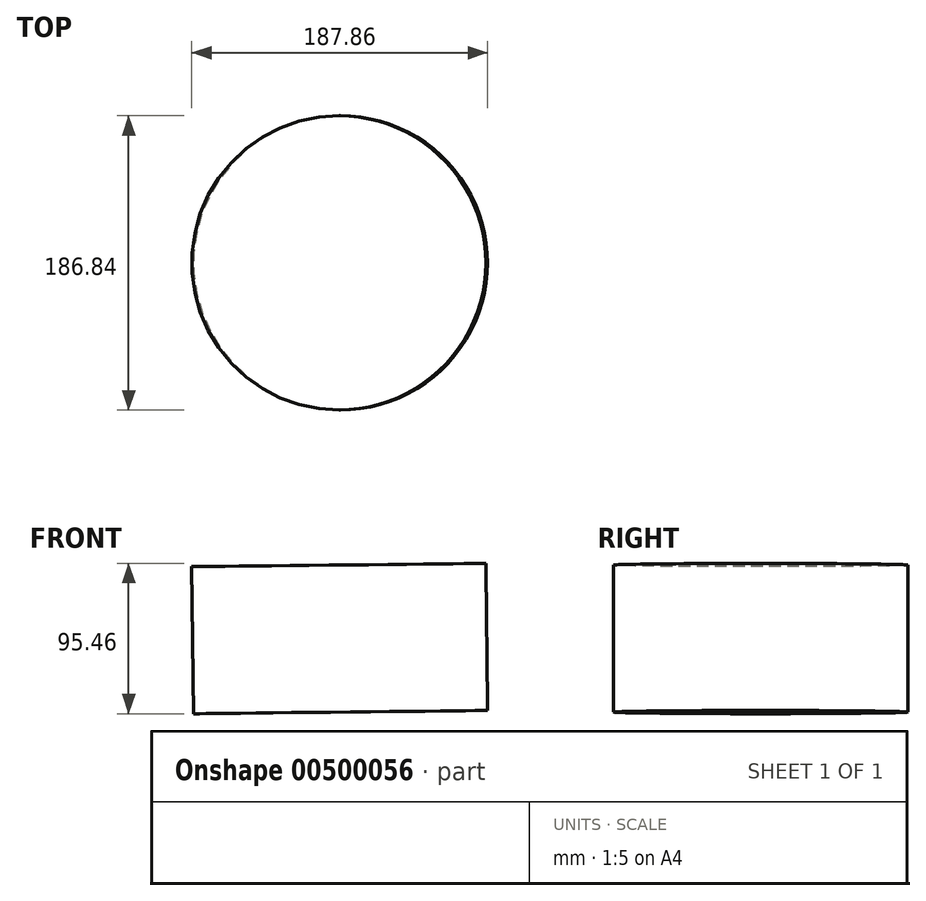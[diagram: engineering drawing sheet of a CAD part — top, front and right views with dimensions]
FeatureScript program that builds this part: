
annotation { "Feature Type Name" : "Feature", "Feature Type Description" : "" }
export const myFeature = defineFeature(function(context is Context, id is Id, definition is map)
    precondition{}
    {
        {
            var Q0;
            Q0=qCreatedBy(makeId("Front.planeOp"),FACE);
            var sketch = newSketch(context, id + "F0", { "sketchPlane" : qUnion([Q0])});
            skCircle(sketch, "E0.cCircle", {"center": v(0, 0) * mm, "radius": 66.06 * mm, "construction": true});
            skLineSegment(sketch, "E0.0", {"start": v(46.2, 47.22) * mm, "end": v(47.22, -46.2) * mm});
            skLineSegment(sketch, "E0.1", {"start": v(47.22, -46.2) * mm, "end": v(-46.2, -47.22) * mm});
            skLineSegment(sketch, "E0.2", {"start": v(-46.2, -47.22) * mm, "end": v(-47.22, 46.2) * mm});
            skLineSegment(sketch, "E0.3", {"start": v(-47.22, 46.2) * mm, "end": v(46.2, 47.22) * mm});
            skSolve(sketch);
        }
        {
            var Q0;
            Q0=makeQuery(id+"F0.imprint","IMPRINT",FACE,{"disambiguationData":[TD([[makeQuery(id+"F0.imprint","IMPRINT",EDGE,{"derivedFrom":sQuery(id+"F0.wireOp",EDGE,"E0.0")}),-1.0]])]});
            var Q1;
            Q1=sQuery(id+"F0.wireOp",EDGE,"E0.0");
            revolve(context, id + "F1", {"entities" : qUnion([Q0]), "axis" : qUnion([Q1]), "revolveType" : RevolveType.FULL});
        }
    });
